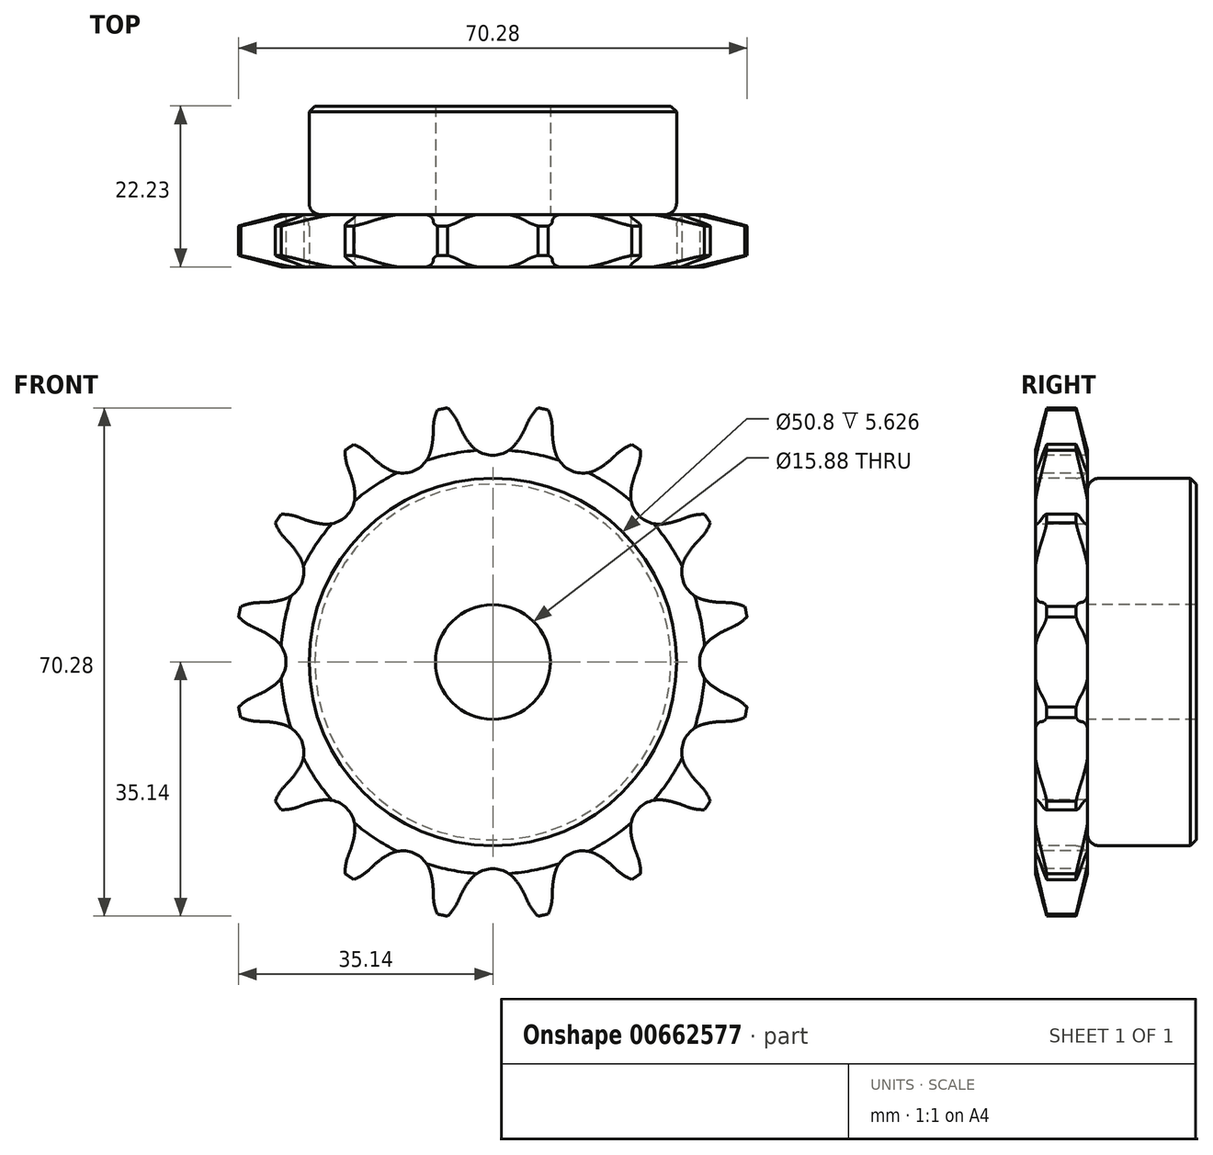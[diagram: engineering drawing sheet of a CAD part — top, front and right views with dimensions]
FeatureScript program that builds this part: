
annotation { "Feature Type Name" : "Feature", "Feature Type Description" : "" }
export const myFeature = defineFeature(function(context is Context, id is Id, definition is map)
    precondition{}
    {
        {
            var Q0;
            Q0=qCreatedBy(makeId("Right.planeOp"),FACE);
            var sketch = newSketch(context, id + "F0", { "sketchPlane" : qUnion([Q0])});
            skLineSegment(sketch, "E0", {"start": v(0, 0) * mm, "end": v(22.35, 0) * mm, "construction": true});
            skLineSegment(sketch, "E1.bottom", {"start": v(0, 7.94) * mm, "end": v(7.21, 7.94) * mm});
            skLineSegment(sketch, "E1.top", {"start": v(0, 35.69) * mm, "end": v(7.21, 35.69) * mm});
            skLineSegment(sketch, "E1.left", {"start": v(0, 7.94) * mm, "end": v(0, 35.69) * mm});
            skLineSegment(sketch, "E1.right", {"start": v(7.21, 7.94) * mm, "end": v(7.21, 35.69) * mm});
            skLineSegment(sketch, "E2.bottom", {"start": v(0, 7.94) * mm, "end": v(22.23, 7.94) * mm});
            skLineSegment(sketch, "E2.top", {"start": v(0, 25.4) * mm, "end": v(22.23, 25.4) * mm});
            skLineSegment(sketch, "E2.left", {"start": v(0, 7.94) * mm, "end": v(0, 25.4) * mm});
            skLineSegment(sketch, "E2.right", {"start": v(22.23, 7.94) * mm, "end": v(22.22, 25.4) * mm});
            skLineSegment(sketch, "E3.MirrorCS", {"start": v(0, -7.94) * mm, "end": v(7.21, -7.94) * mm});
            skLineSegment(sketch, "E4.MirrorCS", {"start": v(22.23, -7.94) * mm, "end": v(22.23, -25.4) * mm});
            skLineSegment(sketch, "E5.MirrorCS", {"start": v(0, -7.94) * mm, "end": v(0, -25.4) * mm});
            skLineSegment(sketch, "E6.MirrorCS", {"start": v(0, -35.69) * mm, "end": v(7.21, -35.69) * mm});
            skLineSegment(sketch, "E7.MirrorCS", {"start": v(0, -7.94) * mm, "end": v(0, -35.69) * mm});
            skLineSegment(sketch, "E8.MirrorCS", {"start": v(7.21, -7.94) * mm, "end": v(7.21, -35.69) * mm});
            skLineSegment(sketch, "E9.MirrorCS", {"start": v(0, -7.94) * mm, "end": v(22.23, -7.94) * mm});
            skLineSegment(sketch, "E10.MirrorCS", {"start": v(0, -25.4) * mm, "end": v(22.23, -25.4) * mm});
            skSolve(sketch);
        }
        {
            var Q0;
            {var subQ5=sQuery(id+"F0.wireOp",EDGE,"E2.left");Q0=makeQuery(id+"F0.imprint","IMPRINT",FACE,{"disambiguationData":[TD([[makeQuery(id+"F0.imprint","IMPRINT",EDGE,{"derivedFrom":subQ5}),-1.0]])]});}
            var Q1;
            {var subQ0=sQuery(id+"F0.wireOp",EDGE,"E1.top");Q1=makeQuery(id+"F0.imprint","IMPRINT",FACE,{"disambiguationData":[TD([[makeQuery(id+"F0.imprint","IMPRINT",EDGE,{"derivedFrom":subQ0}),-1.0]])]});}
            var Q2;
            {var subQ5=sQuery(id+"F0.wireOp",EDGE,"E2.right");Q2=makeQuery(id+"F0.imprint","IMPRINT",FACE,{"disambiguationData":[TD([[makeQuery(id+"F0.imprint","IMPRINT",EDGE,{"derivedFrom":subQ5}),1.0]])]});}
            var Q3;
            Q3=sQuery(id+"F0.wireOp",EDGE,"E0");
            revolve(context, id + "F1", {"entities" : qUnion([Q0, Q1, Q2]), "axis" : qUnion([Q3]), "revolveType" : RevolveType.FULL});
        }
        {
            var Q0;
            Q0=makeQuery(id+"F1.opRevolve","SWEPT_EDGE",EDGE,{"disambiguationData":[OSD([sQuery(id+"F0.wireOp",EDGE,"E1.right"),sQuery(id+"F0.wireOp",EDGE,"E2.top")])]});
            fillet(context, id + "F2", {"entities" : qUnion([Q0]), "radius" : 1.59 * mm, "tangentPropagation" : true, "allowEdgeOverflow" : false});
        }
        {
            var Q0;
            Q0=makeQuery(id+"F1.opRevolve","SWEPT_EDGE",EDGE,{"disambiguationData":[OSD([sQuery(id+"F0.wireOp",EDGE,"E2.top"),sQuery(id+"F0.wireOp",EDGE,"E2.right")])]});
            chamfer(context, id + "F3", {"entities" : qUnion([Q0]), "width" : 0.8 * mm, "tangentPropagation" : true});
        }
        {
            var Q0;
            Q0=makeQuery(id+"F1.opRevolve","SWEPT_EDGE",EDGE,{"disambiguationData":[OSD([sQuery(id+"F0.wireOp",EDGE,"E1.top"),sQuery(id+"F0.wireOp",EDGE,"E1.left")])]});
            var Q1;
            Q1=makeQuery(id+"F1.opRevolve","SWEPT_EDGE",EDGE,{"disambiguationData":[OSD([sQuery(id+"F0.wireOp",EDGE,"E1.top"),sQuery(id+"F0.wireOp",EDGE,"E1.right")])]});
            chamfer(context, id + "F4", {"entities" : qUnion([Q0, Q1]), "chamferType" : ChamferType.TWO_OFFSETS, "width1" : 6.35 * mm, "oppositeDirection" : false, "width2" : 1.57 * mm, "tangentPropagation" : true});
        }
        {
            var Q0;
            Q0=makeQuery(id+"F1.opRevolve","SWEPT_FACE",FACE,{"disambiguationData":[OSD([sQuery(id+"F0.wireOp",EDGE,"E1.left"),sQuery(id+"F0.wireOp",EDGE,"E2.left")])]});
            var sketch = newSketch(context, id + "F5", { "sketchPlane" : qUnion([Q0])});
            skCircle(sketch, "E11", {"center": v(0, 0) * mm, "radius": 32.55 * mm, "construction": true});
            skLineSegment(sketch, "E12", {"start": v(0, 0) * mm, "end": v(0, 32.55) * mm, "construction": true});
            skLineSegment(sketch, "E13", {"start": v(60.75, 32.55) * mm, "end": v(0, 32.55) * mm, "construction": true});
            skLineSegment(sketch, "E14", {"start": v(0, 32.55) * mm, "end": v(5, 36.56) * mm, "construction": true});
            skLineSegment(sketch, "E15", {"start": v(5, 36.56) * mm, "end": v(-4.46, 32.3) * mm, "construction": true});
            skLineSegment(sketch, "E16", {"start": v(-4.46, 32.3) * mm, "end": v(-4.82, 33.1) * mm});
            skLineSegment(sketch, "E17", {"start": v(0, 0) * mm, "end": v(-7.13, 35.85) * mm, "construction": true});
            skArc(sketch, "E18", {"start": v(-7.13, 35.85) * mm, "mid": v(-15.87, 26.15) * mm, "end": v(-4.82, 33.1) * mm, "construction": true});
            skArc(sketch, "E19", {"start": v(-4.82, 33.1) * mm, "mid": v(-5.78, 34.63) * mm, "end": v(-7.13, 35.85) * mm});
            skLineSegment(sketch, "E20", {"start": v(-4.82, 33.1) * mm, "end": v(-8.3, 40.83) * mm, "construction": true});
            skArc(sketch, "E21", {"start": v(-4.46, 32.3) * mm, "mid": v(-3.84, 31.14) * mm, "end": v(-3.1, 30.07) * mm});
            skArc(sketch, "E22", {"start": v(-3.1, 30.07) * mm, "mid": v(13.83, 41.97) * mm, "end": v(-4.46, 32.3) * mm, "construction": true});
            skArc(sketch, "E23.MirrorCS", {"start": v(4.46, 32.3) * mm, "mid": v(3.84, 31.14) * mm, "end": v(3.1, 30.07) * mm});
            skArc(sketch, "E24.MirrorCS", {"start": v(4.82, 33.1) * mm, "mid": v(5.78, 34.63) * mm, "end": v(7.13, 35.85) * mm});
            skLineSegment(sketch, "E25.MirrorCS", {"start": v(4.46, 32.3) * mm, "end": v(4.82, 33.1) * mm});
            skLineSegment(sketch, "E26", {"start": v(-3.1, 30.07) * mm, "end": v(-3.1, 30.07) * mm});
            skLineSegment(sketch, "E27", {"start": v(3.1, 30.07) * mm, "end": v(3.1, 30.07) * mm});
            skArc(sketch, "E28", {"start": v(-3.1, 30.07) * mm, "mid": v(0, 28.59) * mm, "end": v(3.1, 30.07) * mm});
            skArc(sketch, "E29", {"start": v(3.1, 30.07) * mm, "mid": v(0, 36.51) * mm, "end": v(-3.1, 30.07) * mm, "construction": true});
            skArc(sketch, "E30.1.0", {"start": v(-17.12, 28.74) * mm, "mid": v(-18.6, 29.79) * mm, "end": v(-20.3, 30.4) * mm});
            skArc(sketch, "E30.1.1", {"start": v(-14.36, 26.6) * mm, "mid": v(-10.94, 26.41) * mm, "end": v(-8.65, 28.96) * mm});
            skArc(sketch, "E30.1.2", {"start": v(-8.24, 31.55) * mm, "mid": v(-8.37, 30.24) * mm, "end": v(-8.65, 28.96) * mm});
            skArc(sketch, "E30.1.3", {"start": v(-8.22, 32.42) * mm, "mid": v(-7.91, 34.21) * mm, "end": v(-7.13, 35.85) * mm});
            skLineSegment(sketch, "E30.1.4", {"start": v(-8.24, 31.55) * mm, "end": v(-8.22, 32.42) * mm});
            skArc(sketch, "E30.1.5", {"start": v(-16.48, 28.14) * mm, "mid": v(-15.47, 27.3) * mm, "end": v(-14.36, 26.6) * mm});
            skLineSegment(sketch, "E30.1.6", {"start": v(-16.48, 28.14) * mm, "end": v(-17.12, 28.74) * mm});
            skArc(sketch, "E30.2.0", {"start": v(-26.8, 20) * mm, "mid": v(-28.58, 20.4) * mm, "end": v(-30.4, 20.3) * mm});
            skArc(sketch, "E30.2.1", {"start": v(-23.45, 19.08) * mm, "mid": v(-20.21, 20.21) * mm, "end": v(-19.08, 23.45) * mm});
            skArc(sketch, "E30.2.2", {"start": v(-19.69, 26) * mm, "mid": v(-19.3, 24.74) * mm, "end": v(-19.08, 23.45) * mm});
            skArc(sketch, "E30.2.3", {"start": v(-20, 26.8) * mm, "mid": v(-20.4, 28.58) * mm, "end": v(-20.3, 30.4) * mm});
            skLineSegment(sketch, "E30.2.4", {"start": v(-19.69, 26) * mm, "end": v(-20, 26.8) * mm});
            skArc(sketch, "E30.2.5", {"start": v(-26, 19.69) * mm, "mid": v(-24.74, 19.3) * mm, "end": v(-23.45, 19.08) * mm});
            skLineSegment(sketch, "E30.2.6", {"start": v(-26, 19.69) * mm, "end": v(-26.8, 20) * mm});
            skArc(sketch, "E30.3.0", {"start": v(-32.42, 8.22) * mm, "mid": v(-34.21, 7.91) * mm, "end": v(-35.85, 7.13) * mm});
            skArc(sketch, "E30.3.1", {"start": v(-28.96, 8.65) * mm, "mid": v(-26.41, 10.94) * mm, "end": v(-26.6, 14.36) * mm});
            skArc(sketch, "E30.3.2", {"start": v(-28.14, 16.48) * mm, "mid": v(-27.3, 15.47) * mm, "end": v(-26.6, 14.36) * mm});
            skArc(sketch, "E30.3.3", {"start": v(-28.74, 17.12) * mm, "mid": v(-29.79, 18.6) * mm, "end": v(-30.4, 20.3) * mm});
            skLineSegment(sketch, "E30.3.4", {"start": v(-28.14, 16.48) * mm, "end": v(-28.74, 17.12) * mm});
            skArc(sketch, "E30.3.5", {"start": v(-31.55, 8.24) * mm, "mid": v(-30.24, 8.37) * mm, "end": v(-28.96, 8.65) * mm});
            skLineSegment(sketch, "E30.3.6", {"start": v(-31.55, 8.24) * mm, "end": v(-32.42, 8.22) * mm});
            skArc(sketch, "E30.4.0", {"start": v(-33.1, -4.82) * mm, "mid": v(-34.63, -5.78) * mm, "end": v(-35.85, -7.13) * mm});
            skArc(sketch, "E30.4.1", {"start": v(-30.07, -3.1) * mm, "mid": v(-28.59, 0) * mm, "end": v(-30.07, 3.1) * mm});
            skArc(sketch, "E30.4.2", {"start": v(-32.3, 4.46) * mm, "mid": v(-31.14, 3.84) * mm, "end": v(-30.07, 3.1) * mm});
            skArc(sketch, "E30.4.3", {"start": v(-33.1, 4.82) * mm, "mid": v(-34.63, 5.78) * mm, "end": v(-35.85, 7.13) * mm});
            skLineSegment(sketch, "E30.4.4", {"start": v(-32.3, 4.46) * mm, "end": v(-33.1, 4.82) * mm});
            skArc(sketch, "E30.4.5", {"start": v(-32.3, -4.46) * mm, "mid": v(-31.14, -3.84) * mm, "end": v(-30.07, -3.1) * mm});
            skLineSegment(sketch, "E30.4.6", {"start": v(-32.3, -4.46) * mm, "end": v(-33.1, -4.82) * mm});
            skArc(sketch, "E30.5.0", {"start": v(-28.74, -17.12) * mm, "mid": v(-29.79, -18.6) * mm, "end": v(-30.4, -20.3) * mm});
            skArc(sketch, "E30.5.1", {"start": v(-26.6, -14.36) * mm, "mid": v(-26.41, -10.94) * mm, "end": v(-28.96, -8.65) * mm});
            skArc(sketch, "E30.5.2", {"start": v(-31.55, -8.24) * mm, "mid": v(-30.24, -8.37) * mm, "end": v(-28.96, -8.65) * mm});
            skArc(sketch, "E30.5.3", {"start": v(-32.42, -8.22) * mm, "mid": v(-34.21, -7.91) * mm, "end": v(-35.85, -7.13) * mm});
            skLineSegment(sketch, "E30.5.4", {"start": v(-31.55, -8.24) * mm, "end": v(-32.42, -8.22) * mm});
            skArc(sketch, "E30.5.5", {"start": v(-28.14, -16.48) * mm, "mid": v(-27.3, -15.47) * mm, "end": v(-26.6, -14.36) * mm});
            skLineSegment(sketch, "E30.5.6", {"start": v(-28.14, -16.48) * mm, "end": v(-28.74, -17.12) * mm});
            skArc(sketch, "E30.6.0", {"start": v(-20, -26.8) * mm, "mid": v(-20.4, -28.58) * mm, "end": v(-20.3, -30.4) * mm});
            skArc(sketch, "E30.6.1", {"start": v(-19.08, -23.45) * mm, "mid": v(-20.21, -20.21) * mm, "end": v(-23.45, -19.08) * mm});
            skArc(sketch, "E30.6.2", {"start": v(-26, -19.69) * mm, "mid": v(-24.74, -19.3) * mm, "end": v(-23.45, -19.08) * mm});
            skArc(sketch, "E30.6.3", {"start": v(-26.8, -20) * mm, "mid": v(-28.58, -20.4) * mm, "end": v(-30.4, -20.3) * mm});
            skLineSegment(sketch, "E30.6.4", {"start": v(-26, -19.69) * mm, "end": v(-26.8, -20) * mm});
            skArc(sketch, "E30.6.5", {"start": v(-19.69, -26) * mm, "mid": v(-19.3, -24.74) * mm, "end": v(-19.08, -23.45) * mm});
            skLineSegment(sketch, "E30.6.6", {"start": v(-19.69, -26) * mm, "end": v(-20, -26.8) * mm});
            skArc(sketch, "E30.7.0", {"start": v(-8.22, -32.42) * mm, "mid": v(-7.91, -34.21) * mm, "end": v(-7.13, -35.85) * mm});
            skArc(sketch, "E30.7.1", {"start": v(-8.65, -28.96) * mm, "mid": v(-10.94, -26.41) * mm, "end": v(-14.36, -26.6) * mm});
            skArc(sketch, "E30.7.2", {"start": v(-16.48, -28.14) * mm, "mid": v(-15.47, -27.3) * mm, "end": v(-14.36, -26.6) * mm});
            skArc(sketch, "E30.7.3", {"start": v(-17.12, -28.74) * mm, "mid": v(-18.6, -29.79) * mm, "end": v(-20.3, -30.4) * mm});
            skLineSegment(sketch, "E30.7.4", {"start": v(-16.48, -28.14) * mm, "end": v(-17.12, -28.74) * mm});
            skArc(sketch, "E30.7.5", {"start": v(-8.24, -31.55) * mm, "mid": v(-8.37, -30.24) * mm, "end": v(-8.65, -28.96) * mm});
            skLineSegment(sketch, "E30.7.6", {"start": v(-8.24, -31.55) * mm, "end": v(-8.22, -32.42) * mm});
            skArc(sketch, "E30.8.0", {"start": v(4.82, -33.1) * mm, "mid": v(5.78, -34.63) * mm, "end": v(7.13, -35.85) * mm});
            skArc(sketch, "E30.8.1", {"start": v(3.1, -30.07) * mm, "mid": v(0, -28.59) * mm, "end": v(-3.1, -30.07) * mm});
            skArc(sketch, "E30.8.2", {"start": v(-4.46, -32.3) * mm, "mid": v(-3.84, -31.14) * mm, "end": v(-3.1, -30.07) * mm});
            skArc(sketch, "E30.8.3", {"start": v(-4.82, -33.1) * mm, "mid": v(-5.78, -34.63) * mm, "end": v(-7.13, -35.85) * mm});
            skLineSegment(sketch, "E30.8.4", {"start": v(-4.46, -32.3) * mm, "end": v(-4.82, -33.1) * mm});
            skArc(sketch, "E30.8.5", {"start": v(4.46, -32.3) * mm, "mid": v(3.84, -31.14) * mm, "end": v(3.1, -30.07) * mm});
            skLineSegment(sketch, "E30.8.6", {"start": v(4.46, -32.3) * mm, "end": v(4.82, -33.1) * mm});
            skArc(sketch, "E30.9.0", {"start": v(17.12, -28.74) * mm, "mid": v(18.6, -29.79) * mm, "end": v(20.3, -30.4) * mm});
            skArc(sketch, "E30.9.1", {"start": v(14.36, -26.6) * mm, "mid": v(10.94, -26.41) * mm, "end": v(8.65, -28.96) * mm});
            skArc(sketch, "E30.9.2", {"start": v(8.24, -31.55) * mm, "mid": v(8.37, -30.24) * mm, "end": v(8.65, -28.96) * mm});
            skArc(sketch, "E30.9.3", {"start": v(8.22, -32.42) * mm, "mid": v(7.91, -34.21) * mm, "end": v(7.13, -35.85) * mm});
            skLineSegment(sketch, "E30.9.4", {"start": v(8.24, -31.55) * mm, "end": v(8.22, -32.42) * mm});
            skArc(sketch, "E30.9.5", {"start": v(16.48, -28.14) * mm, "mid": v(15.47, -27.3) * mm, "end": v(14.36, -26.6) * mm});
            skLineSegment(sketch, "E30.9.6", {"start": v(16.48, -28.14) * mm, "end": v(17.12, -28.74) * mm});
            skArc(sketch, "E30.10.0", {"start": v(26.8, -20) * mm, "mid": v(28.58, -20.4) * mm, "end": v(30.4, -20.3) * mm});
            skArc(sketch, "E30.10.1", {"start": v(23.45, -19.08) * mm, "mid": v(20.21, -20.21) * mm, "end": v(19.08, -23.45) * mm});
            skArc(sketch, "E30.10.2", {"start": v(19.69, -26) * mm, "mid": v(19.3, -24.74) * mm, "end": v(19.08, -23.45) * mm});
            skArc(sketch, "E30.10.3", {"start": v(20, -26.8) * mm, "mid": v(20.4, -28.58) * mm, "end": v(20.3, -30.4) * mm});
            skLineSegment(sketch, "E30.10.4", {"start": v(19.69, -26) * mm, "end": v(20, -26.8) * mm});
            skArc(sketch, "E30.10.5", {"start": v(26, -19.69) * mm, "mid": v(24.74, -19.3) * mm, "end": v(23.45, -19.08) * mm});
            skLineSegment(sketch, "E30.10.6", {"start": v(26, -19.69) * mm, "end": v(26.8, -20) * mm});
            skArc(sketch, "E30.11.0", {"start": v(32.42, -8.22) * mm, "mid": v(34.21, -7.91) * mm, "end": v(35.85, -7.13) * mm});
            skArc(sketch, "E30.11.1", {"start": v(28.96, -8.65) * mm, "mid": v(26.41, -10.94) * mm, "end": v(26.6, -14.36) * mm});
            skArc(sketch, "E30.11.2", {"start": v(28.14, -16.48) * mm, "mid": v(27.3, -15.47) * mm, "end": v(26.6, -14.36) * mm});
            skArc(sketch, "E30.11.3", {"start": v(28.74, -17.12) * mm, "mid": v(29.79, -18.6) * mm, "end": v(30.4, -20.3) * mm});
            skLineSegment(sketch, "E30.11.4", {"start": v(28.14, -16.48) * mm, "end": v(28.74, -17.12) * mm});
            skArc(sketch, "E30.11.5", {"start": v(31.55, -8.24) * mm, "mid": v(30.24, -8.37) * mm, "end": v(28.96, -8.65) * mm});
            skLineSegment(sketch, "E30.11.6", {"start": v(31.55, -8.24) * mm, "end": v(32.42, -8.22) * mm});
            skArc(sketch, "E30.12.0", {"start": v(33.1, 4.82) * mm, "mid": v(34.63, 5.78) * mm, "end": v(35.85, 7.13) * mm});
            skArc(sketch, "E30.12.1", {"start": v(30.07, 3.1) * mm, "mid": v(28.59, 0) * mm, "end": v(30.07, -3.1) * mm});
            skArc(sketch, "E30.12.2", {"start": v(32.3, -4.46) * mm, "mid": v(31.14, -3.84) * mm, "end": v(30.07, -3.1) * mm});
            skArc(sketch, "E30.12.3", {"start": v(33.1, -4.82) * mm, "mid": v(34.63, -5.78) * mm, "end": v(35.85, -7.13) * mm});
            skLineSegment(sketch, "E30.12.4", {"start": v(32.3, -4.46) * mm, "end": v(33.1, -4.82) * mm});
            skArc(sketch, "E30.12.5", {"start": v(32.3, 4.46) * mm, "mid": v(31.14, 3.84) * mm, "end": v(30.07, 3.1) * mm});
            skLineSegment(sketch, "E30.12.6", {"start": v(32.3, 4.46) * mm, "end": v(33.1, 4.82) * mm});
            skArc(sketch, "E30.13.0", {"start": v(28.74, 17.12) * mm, "mid": v(29.79, 18.6) * mm, "end": v(30.4, 20.3) * mm});
            skArc(sketch, "E30.13.1", {"start": v(26.6, 14.36) * mm, "mid": v(26.41, 10.94) * mm, "end": v(28.96, 8.65) * mm});
            skArc(sketch, "E30.13.2", {"start": v(31.55, 8.24) * mm, "mid": v(30.24, 8.37) * mm, "end": v(28.96, 8.65) * mm});
            skArc(sketch, "E30.13.3", {"start": v(32.42, 8.22) * mm, "mid": v(34.21, 7.91) * mm, "end": v(35.85, 7.13) * mm});
            skLineSegment(sketch, "E30.13.4", {"start": v(31.55, 8.24) * mm, "end": v(32.42, 8.22) * mm});
            skArc(sketch, "E30.13.5", {"start": v(28.14, 16.48) * mm, "mid": v(27.3, 15.47) * mm, "end": v(26.6, 14.36) * mm});
            skLineSegment(sketch, "E30.13.6", {"start": v(28.14, 16.48) * mm, "end": v(28.74, 17.12) * mm});
            skArc(sketch, "E30.14.0", {"start": v(20, 26.8) * mm, "mid": v(20.4, 28.58) * mm, "end": v(20.3, 30.4) * mm});
            skArc(sketch, "E30.14.1", {"start": v(19.08, 23.45) * mm, "mid": v(20.21, 20.21) * mm, "end": v(23.45, 19.08) * mm});
            skArc(sketch, "E30.14.2", {"start": v(26, 19.69) * mm, "mid": v(24.74, 19.3) * mm, "end": v(23.45, 19.08) * mm});
            skArc(sketch, "E30.14.3", {"start": v(26.8, 20) * mm, "mid": v(28.58, 20.4) * mm, "end": v(30.4, 20.3) * mm});
            skLineSegment(sketch, "E30.14.4", {"start": v(26, 19.69) * mm, "end": v(26.8, 20) * mm});
            skArc(sketch, "E30.14.5", {"start": v(19.69, 26) * mm, "mid": v(19.3, 24.74) * mm, "end": v(19.08, 23.45) * mm});
            skLineSegment(sketch, "E30.14.6", {"start": v(19.69, 26) * mm, "end": v(20, 26.8) * mm});
            skArc(sketch, "E30.15.0", {"start": v(8.22, 32.42) * mm, "mid": v(7.91, 34.21) * mm, "end": v(7.13, 35.85) * mm});
            skArc(sketch, "E30.15.1", {"start": v(8.65, 28.96) * mm, "mid": v(10.94, 26.41) * mm, "end": v(14.36, 26.6) * mm});
            skArc(sketch, "E30.15.2", {"start": v(16.48, 28.14) * mm, "mid": v(15.47, 27.3) * mm, "end": v(14.36, 26.6) * mm});
            skArc(sketch, "E30.15.3", {"start": v(17.12, 28.74) * mm, "mid": v(18.6, 29.79) * mm, "end": v(20.3, 30.4) * mm});
            skLineSegment(sketch, "E30.15.4", {"start": v(16.48, 28.14) * mm, "end": v(17.12, 28.74) * mm});
            skArc(sketch, "E30.15.5", {"start": v(8.24, 31.55) * mm, "mid": v(8.37, 30.24) * mm, "end": v(8.65, 28.96) * mm});
            skLineSegment(sketch, "E30.15.6", {"start": v(8.24, 31.55) * mm, "end": v(8.22, 32.42) * mm});
            skSolve(sketch);
        }
        {
            var Q0;
            Q0 = qSketchRegion(id + "F5", true);
            extrude(context, id + "F6", {"entities" : qUnion([Q0]), "operationType" : NewBodyOperationType.INTERSECT, "oppositeDirection" : true, "depth" : 25.4 * mm, "offsetDistance" : 25.4 * mm});
        }
    });
